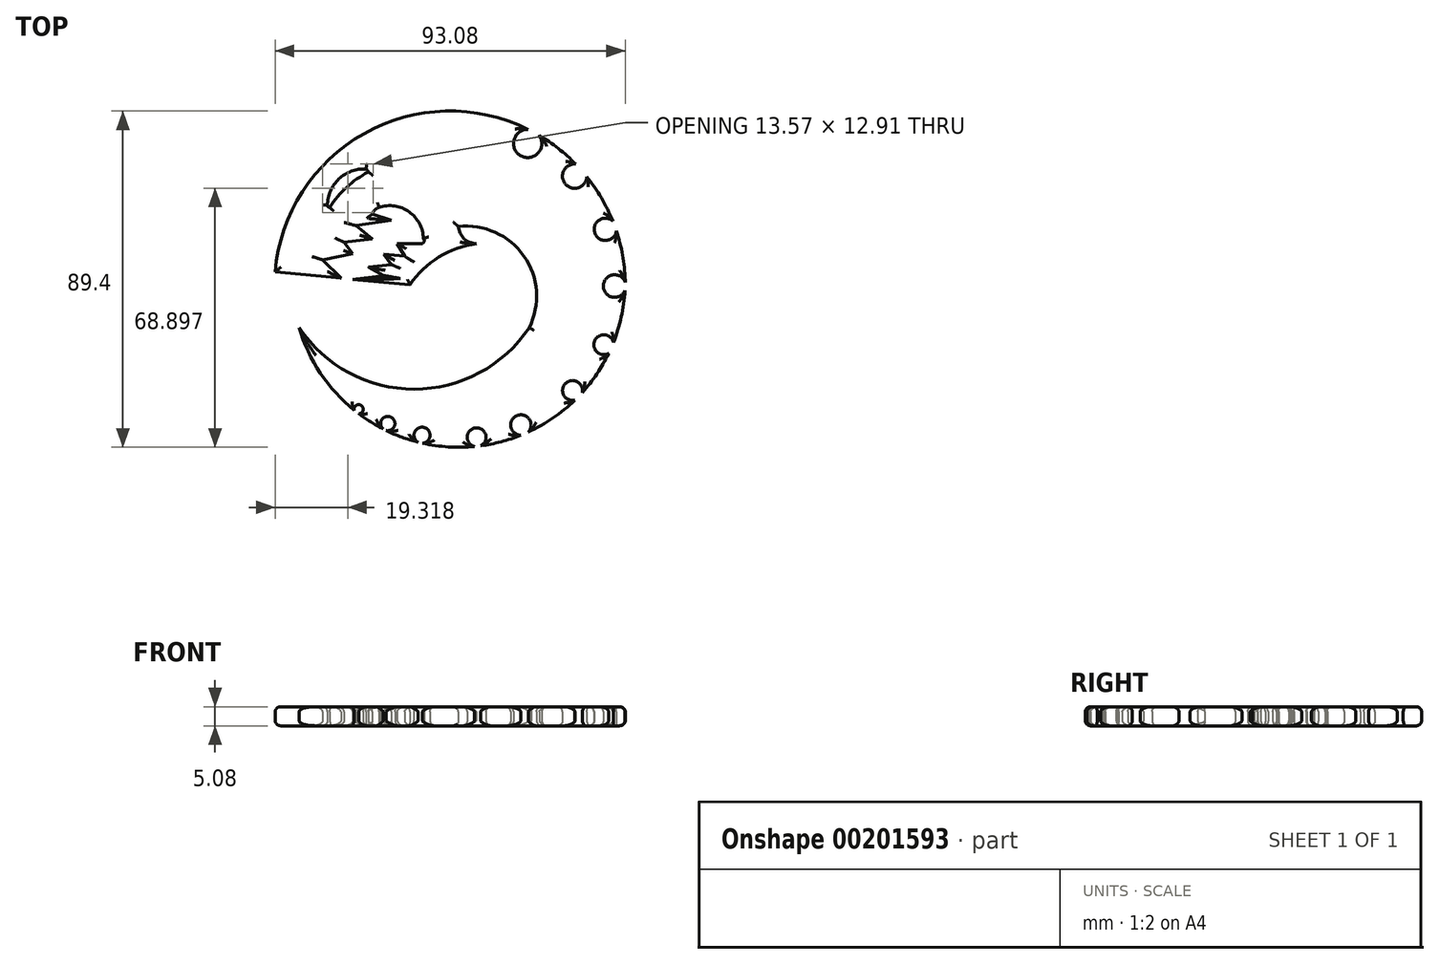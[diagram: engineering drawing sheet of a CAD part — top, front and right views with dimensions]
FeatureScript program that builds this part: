
annotation { "Feature Type Name" : "Feature", "Feature Type Description" : "" }
export const myFeature = defineFeature(function(context is Context, id is Id, definition is map)
    precondition{}
    {
        {
            var Q0;
            Q0=qCreatedBy(makeId("Top.planeOp"),FACE);
            var sketch = newSketch(context, id + "F0", { "sketchPlane" : qUnion([Q0])});
            skArc(sketch, "E0", {"start": v(45.94, 5.65) * mm, "mid": v(45.22, 12.27) * mm, "end": v(43.57, 18.72) * mm});
            skPoint(sketch, "E0.startSnap0", {"position": v(48.89, 5.65) * mm});
            skArc(sketch, "E1", {"start": v(-40.78, -7) * mm, "mid": v(-35.13, -19.1) * mm, "end": v(-26.13, -28.98) * mm});
            skArc(sketch, "E2", {"start": v(-40.78, -7) * mm, "mid": v(-10.2, -23.36) * mm, "end": v(20.4, -7) * mm});
            skArc(sketch, "E3", {"start": v(20.4, -7) * mm, "mid": v(18.98, 12.03) * mm, "end": v(1.57, 19.86) * mm});
            skArc(sketch, "E4", {"start": v(6.39, 15.3) * mm, "mid": v(-3.64, 11.75) * mm, "end": v(-11.3, 4.38) * mm});
            skArc(sketch, "E5", {"start": v(1.57, 19.86) * mm, "mid": v(3.1, 16.65) * mm, "end": v(6.39, 15.3) * mm});
            skArc(sketch, "E6", {"start": v(-7.75, 16.65) * mm, "mid": v(-11.54, 23.78) * mm, "end": v(-19.53, 24.97) * mm});
            skPoint(sketch, "E6.startSnap0", {"position": v(3.1, 16.65) * mm});
            skLineSegment(sketch, "E7", {"start": v(-47.14, 7.84) * mm, "end": v(-29.65, 6.15) * mm});
            skLineSegment(sketch, "E8", {"start": v(-28.8, 15.72) * mm, "end": v(-21.28, 16.6) * mm});
            skLineSegment(sketch, "E9", {"start": v(-21.28, 16.6) * mm, "end": v(-25.6, 20.1) * mm});
            skLineSegment(sketch, "E10", {"start": v(-25.6, 20.1) * mm, "end": v(-16.22, 21.57) * mm});
            skLineSegment(sketch, "E11", {"start": v(-16.22, 21.57) * mm, "end": v(-21.28, 23.13) * mm});
            skLineSegment(sketch, "E12", {"start": v(-22.38, 9.05) * mm, "end": v(-16.3, 9.8) * mm});
            skLineSegment(sketch, "E13", {"start": v(-16.3, 9.8) * mm, "end": v(-18.3, 12.52) * mm});
            skLineSegment(sketch, "E14", {"start": v(-18.3, 12.52) * mm, "end": v(-12.7, 11.98) * mm});
            skLineSegment(sketch, "E15", {"start": v(-12.7, 11.98) * mm, "end": v(-14.68, 15.32) * mm});
            skLineSegment(sketch, "E16", {"start": v(-14.68, 15.32) * mm, "end": v(-8.3, 15.32) * mm});
            skLineSegment(sketch, "E17.trimOffspring", {"start": v(-26.55, 5.85) * mm, "end": v(-11.3, 4.38) * mm});
            skLineSegment(sketch, "E18", {"start": v(-26.55, 5.85) * mm, "end": v(-18.28, 6.86) * mm});
            skLineSegment(sketch, "E19", {"start": v(-18.28, 6.86) * mm, "end": v(-22.38, 9.05) * mm});
            skLineSegment(sketch, "E20", {"start": v(-28.8, 15.72) * mm, "end": v(-26.55, 12.6) * mm});
            skLineSegment(sketch, "E21", {"start": v(-26.55, 12.6) * mm, "end": v(-34.53, 11.03) * mm});
            skLineSegment(sketch, "E22", {"start": v(-34.53, 11.03) * mm, "end": v(-29.65, 6.15) * mm});
            skArc(sketch, "E23", {"start": v(-19.53, 24.97) * mm, "mid": v(-20.65, 24.28) * mm, "end": v(-21.28, 23.13) * mm});
            skArc(sketch, "E24", {"start": v(-8.3, 15.32) * mm, "mid": v(-7.59, 15.8) * mm, "end": v(-7.75, 16.65) * mm});
            skArc(sketch, "E25", {"start": v(-23.01, 35.18) * mm, "mid": v(-30.18, 32.54) * mm, "end": v(-33.24, 25.54) * mm});
            skArc(sketch, "E26", {"start": v(-22.4, 34.37) * mm, "mid": v(-22.59, 34.87) * mm, "end": v(-23.01, 35.18) * mm});
            skArc(sketch, "E27", {"start": v(-33.24, 25.54) * mm, "mid": v(-33.09, 25.1) * mm, "end": v(-32.63, 25.02) * mm});
            skArc(sketch, "E28", {"start": v(-22.4, 34.37) * mm, "mid": v(-28.12, 30.35) * mm, "end": v(-32.63, 25.02) * mm});
            skArc(sketch, "E29", {"start": v(20.1, 45.71) * mm, "mid": v(18.19, 38.66) * mm, "end": v(23.07, 44.1) * mm});
            skArc(sketch, "E30", {"start": v(32.73, 36.5) * mm, "mid": v(30.05, 31.14) * mm, "end": v(35.7, 33.14) * mm});
            skArc(sketch, "E31", {"start": v(42.6, 21.34) * mm, "mid": v(37.86, 18.1) * mm, "end": v(43.57, 18.72) * mm});
            skArc(sketch, "E32", {"start": v(45.94, 5.07) * mm, "mid": v(40.12, 4.15) * mm, "end": v(45.86, 2.84) * mm});
            skArc(sketch, "E33", {"start": v(42.8, -10.93) * mm, "mid": v(37.8, -10.48) * mm, "end": v(41.5, -13.86) * mm});
            skArc(sketch, "E34", {"start": v(-7.99, -37.74) * mm, "mid": v(-7.62, -33.54) * mm, "end": v(-9.19, -37.45) * mm});
            skArc(sketch, "E35", {"start": v(-17.63, -34.37) * mm, "mid": v(-16.36, -30.81) * mm, "end": v(-18.43, -33.97) * mm});
            skArc(sketch, "E36", {"start": v(-24.94, -29.9) * mm, "mid": v(-24.2, -27.74) * mm, "end": v(-26.13, -28.98) * mm});
            skArc(sketch, "E37.trimOffspring", {"start": v(20.1, 45.71) * mm, "mid": v(-23.55, 44.59) * mm, "end": v(-47.14, 7.84) * mm});
            skArc(sketch, "E38.trimOffspring", {"start": v(32.73, 36.5) * mm, "mid": v(28.15, 40.62) * mm, "end": v(23.07, 44.1) * mm});
            skArc(sketch, "E39.trimOffspring", {"start": v(42.6, 21.34) * mm, "mid": v(39.6, 27.5) * mm, "end": v(35.7, 33.14) * mm});
            skArc(sketch, "E40.trimOffspring", {"start": v(45.94, 5.07) * mm, "mid": v(45.94, 5.36) * mm, "end": v(45.94, 5.65) * mm});
            skArc(sketch, "E41.trimOffspring", {"start": v(42.8, -10.93) * mm, "mid": v(44.88, -4.17) * mm, "end": v(45.86, 2.84) * mm});
            skArc(sketch, "E42.trimOffspring", {"start": v(-7.99, -37.74) * mm, "mid": v(-1.09, -38.72) * mm, "end": v(5.89, -38.61) * mm});
            skArc(sketch, "E43.trimOffspring", {"start": v(-17.63, -34.37) * mm, "mid": v(-13.49, -36.13) * mm, "end": v(-9.19, -37.45) * mm});
            skArc(sketch, "E44.trimOffspring", {"start": v(-24.94, -29.9) * mm, "mid": v(-21.77, -32.08) * mm, "end": v(-18.43, -33.97) * mm});
            skArc(sketch, "E45", {"start": v(34.5, -24.24) * mm, "mid": v(30, -21.88) * mm, "end": v(32.53, -26.3) * mm});
            skArc(sketch, "E46", {"start": v(20.15, -34.77) * mm, "mid": v(17.1, -30.41) * mm, "end": v(18.17, -35.62) * mm});
            skArc(sketch, "E47.trimOffspring", {"start": v(20.15, -34.77) * mm, "mid": v(26.7, -31.06) * mm, "end": v(32.53, -26.3) * mm});
            skArc(sketch, "E48.trimOffspring", {"start": v(34.5, -24.24) * mm, "mid": v(38.38, -19.3) * mm, "end": v(41.5, -13.86) * mm});
            skArc(sketch, "E49", {"start": v(7.48, -38.43) * mm, "mid": v(6.13, -33.66) * mm, "end": v(5.89, -38.61) * mm});
            skArc(sketch, "E50.trimOffspring", {"start": v(7.48, -38.43) * mm, "mid": v(12.92, -37.36) * mm, "end": v(18.17, -35.62) * mm});
            skSolve(sketch);
        }
        {
            var Q0;
            Q0=makeQuery(id+"F0.imprint","IMPRINT",FACE,{"disambiguationData":[TD([[makeQuery(id+"F0.imprint","IMPRINT",EDGE,{"derivedFrom":sQuery(id+"F0.wireOp",EDGE,"E25")}),1.0]])]});
            extrude(context, id + "F1", {"entities" : qUnion([Q0]), "depth" : 76.2 * mm, "symmetric" : true});
        }
        {
            var Q0;
            Q0=makeQuery(id+"F0.imprint","IMPRINT",FACE,{"disambiguationData":[TD([[makeQuery(id+"F0.imprint","IMPRINT",EDGE,{"derivedFrom":sQuery(id+"F0.wireOp",EDGE,"E25")}),1.0]])]});
            var Q1;
            Q1=makeQuery(id+"F0.imprint","IMPRINT",FACE,{"disambiguationData":[TD([[makeQuery(id+"F0.imprint","IMPRINT",EDGE,{"derivedFrom":sQuery(id+"F0.wireOp",EDGE,"uxuGtYRC-gamm-2Of2-8QVJ-o7ytbOf1ASVi")}),1.0]])]});
            var Q2;
            Q2=makeQuery(id+"F0.imprint","IMPRINT",FACE,{"disambiguationData":[TD([[makeQuery(id+"F0.imprint","IMPRINT",EDGE,{"derivedFrom":sQuery(id+"F0.wireOp",EDGE,"E0")}),1.0]])]});
            extrude(context, id + "F2", {"entities" : qUnion([Q0, Q1, Q2]), "depth" : 5.08 * mm});
        }
        {
            var Q0;
            Q0=makeQuery(id+"F1.opExtrude","SWEPT_BODY",BODY,{"disambiguationData":[OSD([sQuery(id+"F0.wireOp",EDGE,"E25"),sQuery(id+"F0.wireOp",EDGE,"E26"),sQuery(id+"F0.wireOp",EDGE,"E27"),sQuery(id+"F0.wireOp",EDGE,"E28")])]});
            var Q1;
            Q1=makeQuery(id+"F2.opExtrude","SWEPT_BODY",BODY,{"disambiguationData":[OSD([sQuery(id+"F0.wireOp",EDGE,"E0"),sQuery(id+"F0.wireOp",EDGE,"E1"),sQuery(id+"F0.wireOp",EDGE,"E2"),sQuery(id+"F0.wireOp",EDGE,"E3"),sQuery(id+"F0.wireOp",EDGE,"E4"),sQuery(id+"F0.wireOp",EDGE,"E5"),sQuery(id+"F0.wireOp",EDGE,"E6"),sQuery(id+"F0.wireOp",EDGE,"E7"),sQuery(id+"F0.wireOp",EDGE,"E8"),sQuery(id+"F0.wireOp",EDGE,"E9"),sQuery(id+"F0.wireOp",EDGE,"E10"),sQuery(id+"F0.wireOp",EDGE,"E11"),sQuery(id+"F0.wireOp",EDGE,"E12"),sQuery(id+"F0.wireOp",EDGE,"E13"),sQuery(id+"F0.wireOp",EDGE,"E14"),sQuery(id+"F0.wireOp",EDGE,"E15"),sQuery(id+"F0.wireOp",EDGE,"E16"),sQuery(id+"F0.wireOp",EDGE,"E17.trimOffspring"),sQuery(id+"F0.wireOp",EDGE,"E18"),sQuery(id+"F0.wireOp",EDGE,"E19"),sQuery(id+"F0.wireOp",EDGE,"E20"),sQuery(id+"F0.wireOp",EDGE,"E21"),sQuery(id+"F0.wireOp",EDGE,"E22"),sQuery(id+"F0.wireOp",EDGE,"E23"),sQuery(id+"F0.wireOp",EDGE,"E24"),sQuery(id+"F0.wireOp",EDGE,"E29"),sQuery(id+"F0.wireOp",EDGE,"E30"),sQuery(id+"F0.wireOp",EDGE,"E31"),sQuery(id+"F0.wireOp",EDGE,"E32"),sQuery(id+"F0.wireOp",EDGE,"E33"),sQuery(id+"F0.wireOp",EDGE,"E34"),sQuery(id+"F0.wireOp",EDGE,"E35"),sQuery(id+"F0.wireOp",EDGE,"E36"),sQuery(id+"F0.wireOp",EDGE,"E37.trimOffspring"),sQuery(id+"F0.wireOp",EDGE,"E38.trimOffspring"),sQuery(id+"F0.wireOp",EDGE,"E39.trimOffspring"),sQuery(id+"F0.wireOp",EDGE,"E40.trimOffspring"),sQuery(id+"F0.wireOp",EDGE,"E41.trimOffspring"),sQuery(id+"F0.wireOp",EDGE,"E42.trimOffspring"),sQuery(id+"F0.wireOp",EDGE,"E43.trimOffspring"),sQuery(id+"F0.wireOp",EDGE,"E44.trimOffspring"),sQuery(id+"F0.wireOp",EDGE,"E45"),sQuery(id+"F0.wireOp",EDGE,"E46"),sQuery(id+"F0.wireOp",EDGE,"E47.trimOffspring"),sQuery(id+"F0.wireOp",EDGE,"E48.trimOffspring")])]});
            booleanBodies(context, id + "F3", {"operationType" : BooleanOperationType.SUBTRACTION, "tools" : qUnion([Q0]), "targets" : qUnion([Q1])});
        }
        {
            var Q0;
            Q0=makeQuery(id+"F2.opExtrude","CAP_FACE",FACE,{"disambiguationData":[OSD([sQuery(id+"F0.wireOp",EDGE,"E0"),sQuery(id+"F0.wireOp",EDGE,"E1"),sQuery(id+"F0.wireOp",EDGE,"E2"),sQuery(id+"F0.wireOp",EDGE,"E3"),sQuery(id+"F0.wireOp",EDGE,"E4"),sQuery(id+"F0.wireOp",EDGE,"E5"),sQuery(id+"F0.wireOp",EDGE,"E6"),sQuery(id+"F0.wireOp",EDGE,"E7"),sQuery(id+"F0.wireOp",EDGE,"E8"),sQuery(id+"F0.wireOp",EDGE,"E9"),sQuery(id+"F0.wireOp",EDGE,"E10"),sQuery(id+"F0.wireOp",EDGE,"E11"),sQuery(id+"F0.wireOp",EDGE,"E12"),sQuery(id+"F0.wireOp",EDGE,"E13"),sQuery(id+"F0.wireOp",EDGE,"E14"),sQuery(id+"F0.wireOp",EDGE,"E15"),sQuery(id+"F0.wireOp",EDGE,"E16"),sQuery(id+"F0.wireOp",EDGE,"E17.trimOffspring"),sQuery(id+"F0.wireOp",EDGE,"E18"),sQuery(id+"F0.wireOp",EDGE,"E19"),sQuery(id+"F0.wireOp",EDGE,"E20"),sQuery(id+"F0.wireOp",EDGE,"E21"),sQuery(id+"F0.wireOp",EDGE,"E22"),sQuery(id+"F0.wireOp",EDGE,"E23"),sQuery(id+"F0.wireOp",EDGE,"E24"),sQuery(id+"F0.wireOp",EDGE,"E29"),sQuery(id+"F0.wireOp",EDGE,"E30"),sQuery(id+"F0.wireOp",EDGE,"E31"),sQuery(id+"F0.wireOp",EDGE,"E32"),sQuery(id+"F0.wireOp",EDGE,"E33"),sQuery(id+"F0.wireOp",EDGE,"E34"),sQuery(id+"F0.wireOp",EDGE,"E35"),sQuery(id+"F0.wireOp",EDGE,"E36"),sQuery(id+"F0.wireOp",EDGE,"E37.trimOffspring"),sQuery(id+"F0.wireOp",EDGE,"E38.trimOffspring"),sQuery(id+"F0.wireOp",EDGE,"E39.trimOffspring"),sQuery(id+"F0.wireOp",EDGE,"E40.trimOffspring"),sQuery(id+"F0.wireOp",EDGE,"E41.trimOffspring"),sQuery(id+"F0.wireOp",EDGE,"E42.trimOffspring"),sQuery(id+"F0.wireOp",EDGE,"E43.trimOffspring"),sQuery(id+"F0.wireOp",EDGE,"E44.trimOffspring"),sQuery(id+"F0.wireOp",EDGE,"E45"),sQuery(id+"F0.wireOp",EDGE,"E46"),sQuery(id+"F0.wireOp",EDGE,"E47.trimOffspring"),sQuery(id+"F0.wireOp",EDGE,"E48.trimOffspring")])],"isStart":false});
            fillet(context, id + "F4", {"entities" : qUnion([Q0]), "radius" : 1.37 * mm, "tangentPropagation" : true, "allowEdgeOverflow" : false});
        }
        {
            var Q0;
            Q0=makeQuery(id+"F2.opExtrude","CAP_FACE",FACE,{"disambiguationData":[OSD([sQuery(id+"F0.wireOp",EDGE,"E0"),sQuery(id+"F0.wireOp",EDGE,"E1"),sQuery(id+"F0.wireOp",EDGE,"E2"),sQuery(id+"F0.wireOp",EDGE,"E3"),sQuery(id+"F0.wireOp",EDGE,"E4"),sQuery(id+"F0.wireOp",EDGE,"E5"),sQuery(id+"F0.wireOp",EDGE,"E6"),sQuery(id+"F0.wireOp",EDGE,"E7"),sQuery(id+"F0.wireOp",EDGE,"E8"),sQuery(id+"F0.wireOp",EDGE,"E9"),sQuery(id+"F0.wireOp",EDGE,"E10"),sQuery(id+"F0.wireOp",EDGE,"E11"),sQuery(id+"F0.wireOp",EDGE,"E12"),sQuery(id+"F0.wireOp",EDGE,"E13"),sQuery(id+"F0.wireOp",EDGE,"E14"),sQuery(id+"F0.wireOp",EDGE,"E15"),sQuery(id+"F0.wireOp",EDGE,"E16"),sQuery(id+"F0.wireOp",EDGE,"E17.trimOffspring"),sQuery(id+"F0.wireOp",EDGE,"E18"),sQuery(id+"F0.wireOp",EDGE,"E19"),sQuery(id+"F0.wireOp",EDGE,"E20"),sQuery(id+"F0.wireOp",EDGE,"E21"),sQuery(id+"F0.wireOp",EDGE,"E22"),sQuery(id+"F0.wireOp",EDGE,"E23"),sQuery(id+"F0.wireOp",EDGE,"E24"),sQuery(id+"F0.wireOp",EDGE,"E29"),sQuery(id+"F0.wireOp",EDGE,"E30"),sQuery(id+"F0.wireOp",EDGE,"E31"),sQuery(id+"F0.wireOp",EDGE,"E32"),sQuery(id+"F0.wireOp",EDGE,"E33"),sQuery(id+"F0.wireOp",EDGE,"E34"),sQuery(id+"F0.wireOp",EDGE,"E35"),sQuery(id+"F0.wireOp",EDGE,"E36"),sQuery(id+"F0.wireOp",EDGE,"E37.trimOffspring"),sQuery(id+"F0.wireOp",EDGE,"E38.trimOffspring"),sQuery(id+"F0.wireOp",EDGE,"E39.trimOffspring"),sQuery(id+"F0.wireOp",EDGE,"E40.trimOffspring"),sQuery(id+"F0.wireOp",EDGE,"E41.trimOffspring"),sQuery(id+"F0.wireOp",EDGE,"E42.trimOffspring"),sQuery(id+"F0.wireOp",EDGE,"E43.trimOffspring"),sQuery(id+"F0.wireOp",EDGE,"E44.trimOffspring"),sQuery(id+"F0.wireOp",EDGE,"E45"),sQuery(id+"F0.wireOp",EDGE,"E46"),sQuery(id+"F0.wireOp",EDGE,"E47.trimOffspring"),sQuery(id+"F0.wireOp",EDGE,"E48.trimOffspring")])],"isStart":true});
            fillet(context, id + "F5", {"entities" : qUnion([Q0]), "radius" : 1.37 * mm, "tangentPropagation" : true, "allowEdgeOverflow" : false});
        }
    });
